# Revit family: PRD_AR_ShwrFttngsPckg_F5SSelfClosingThermostaticMixer_F5ST2037
name_source: partatom
category: Plumbing Fixtures
units: mm (PartAtom-declared; Revit-internal decimal feet)

## family parameters
Cut with Voids When Loaded = No
Enable Cutting in Views = No
Host = Face
Maintain Annotation Orientation = No
OmniClass Number = 23.45.05.14.99
OmniClass Title = Other Sanitary Washing Plumbing Fixtures
Part Type = Normal
Room Calculation Point = No
Round Connector Dimension = Use Diameter
Shared = No

## types (1)
- F5ST2037
    AccentColour = chrome-look (glossy)
    AdditionalConnections = No
    AdditonalMechanism = No
    AdjustableFlowTime = Yes
    AssetType = Fixed
    BIMObjectName = PRD_AR_ ShowerFittingsPackage_F5SSelfClosingThermostaticMixer_F5ST2037
    Base = No
    BasicColour = stainless steel-look
    BodyMaterial = PRD_AR_StainlessSteel_SatinFinished
    BuiltInFittingModel = Finishing section
    CalculationFlowRateColdWater = 0.15 l/s
    CalculationFlowRateHotWater = 0.15 l/s
    Category = Pr_40_20_87_75, Shower fittings package
    Circulation = No
    Color = stainless steel-look
    CompatibleA3000Open = No
    ConnectionWithPayWaterDispenser = not possible
    CoverPlateHeight = 245 mm
    CoverPlateWidth = 190 mm
    DN = 15  [stored 0.0492126 ft]
    Default Elevation = 1200 mm
    DefaultAutomatic HygieneFlush = fixed interval 24 hours
    Description = F5S-Therm self-closing thermostatic mixer DN 15 as finished installation kit for wall mounting in mounting kit, for shower facilities. Hydraulically controlled, connects to hot water and cold water. Function block with integrated FRAMIC self-closing cartridge, thermostat and pre-assembled hygiene unit including sensor with control electronics and 6 V lithium battery (CR-P2) to perform automatic water hygiene flushing, program-controlled thermal disinfection (additional bypass solenoid-operated flush valve cartridge necessary) and storage of statistical data. Additional mechanism for second bypass solenoid valve cartridge for separate rinsing of the cold-water line and separate sampling of cold or hot water. FRAMIC self-closing cartridge, low maintenance and stagnation free, with ceramic disc technology, self closing, flow pressure independent due to medium-independent design. Continuously adjustable flow duration. Thermostat with metal handle with adjustable and turn-proof temperature stop and option for manual thermal disinfection. All-metal construction, visible parts high-polished, chrome-plated. Holding frame including profile seal, stainless steel cover 190 x 245 mm with covered screw fixing, chrome-plated plastic rosettes, non-return valve and strainers. Depth adjustability 25 mm.
    DiameterNominal = DN 15
    DrainSize = 15 mm  [stored 0.0492126 ft]
    Export Type to IFC As = IfcSanitaryTerminalType
    Features = Hydraulically controlled, connects to hot water and cold water. All-metal construction, visible parts high-polished, chrome-plated. Depth adjustability 25 mm.
    Finish = satin finished
    FlowColdWater = 0.2 L/s
    FlowHotWater = 0.2 L/s
    ForHandShower = No
    FunctionalPrinciple = hydraulic self-closing
    HasTray = No
    HygieneFlushing = Yes
    IfcExportAs = IfcSanitaryTerminalType
    IfcExportType = SHOWER
    InletSize = G 3/4 B
    LockingMechanism = Top section, ceramic
    Manufacturer = KWC Group Management AG
    ManufacturerName = KWC Group Management AG
    ManufacturerURL = www.kwc-professional.com
    Material = stainless steel
    MaterialCasing = stainless steel
    MaterialFitting = brass-look
    MaximumFlowTime = 35 Seconds
    MinimumFlowPressure = 1 bar
    MinimumFlowTime = 5 Seconds
    Model = F5ST2037
    ModelNumber = 2030067164
    ModelReference = F5ST2037
    NBSDescription = Shower fittings package
    NBSReference = 45-35-70/330
    Name = F5S Self-closing thermostatic mixer F5ST2037
    NominalDepth = 0 mm  [stored 0 ft]
    NominalHeight = 245 mm  [stored 0.803806 ft]
    NominalLength = 245 mm  [stored 0.803806 ft]
    NominalWidth = 190 mm  [stored 0.62336 ft]
    NumberOfBatteries = 1
    Parameterization = remote control
    PositionOfWaterConnection = from side
    PowerConsumption = 1.5 Voltampere
    PowerSupplyConnection = Battery 6 V
    ProductInformation = http://pim.kwc.com
    ProtectiveShutdown = No
    Sensor = Yes
    ShowerPipeDraining = No
    ShowerType = Individual
    Size = 15
    SoundInsulation = No
    Status = NEW
    Stops = Yes
    SurfaceFinishCasing = satin finished
    SurfaceFinishFitting = chromed
    SurfaceTreatmentFitting = polished
    TemperatureLimit = Yes
    ThermalDisinfection = Yes
    Type IFC Predefined Type = SHOWER
    TypeOfBatteries = CR-P2 Lithium battery 6V
    TypeOfMixing = with thermostat
    TypeOfMounting = in-wall installation with box
    TypeOfOperation = manual operation
    TypeOfPowerSupply = Battery
    TypeOfSensor = opto-electronic sensor
    TypeOfShower = in-wall fitting
    URL = www.kwc-professional.com
    Uniclass2015Code = Pr_40_20_87_75
    Uniclass2015Title = Shower fittings package
    Uniclass2015Version = Products v1.36
    Version = 1
    VolumeFlowRateAt3Bar = 0.2 l/s
    WaterConnection = threaded connection (external)
    WithBackflowPreventer = Yes
    WithFilter = Yes
    WithRosettesCoverPlate = Yes
    WithTransformerPowerSupply = No

note: [stored X ft] marks values corroborated as IEEE doubles in the binary element streams (Revit-internal decimal feet)

## geometry (parser evidence)
native form markers: Sweep x5
no freeform markers — native parametric forms only
